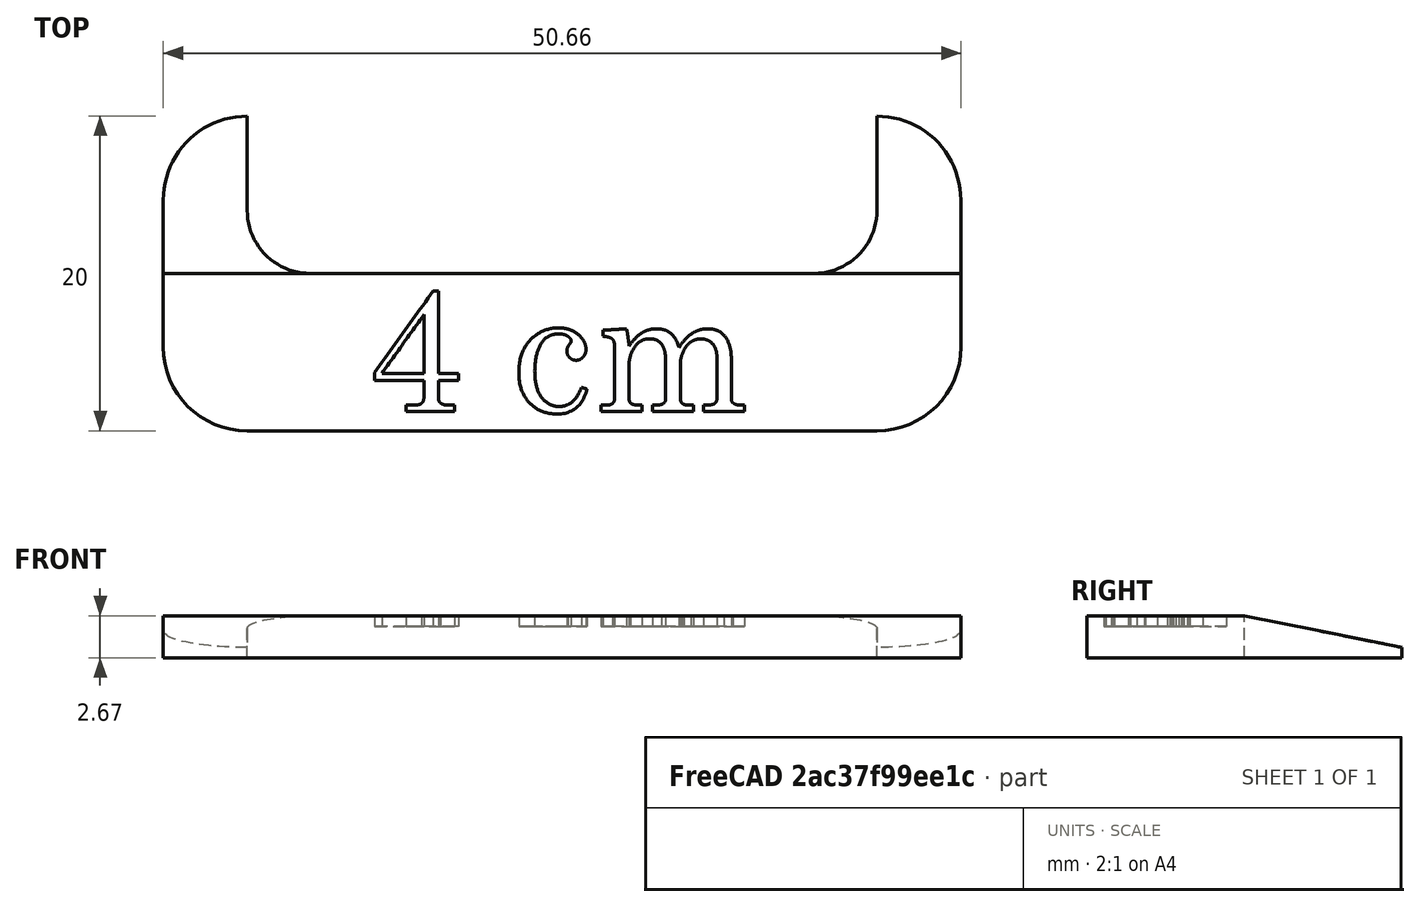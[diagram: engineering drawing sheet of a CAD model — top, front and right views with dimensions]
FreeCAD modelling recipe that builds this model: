
FCSTD DOCUMENT  (FreeCAD 0.20R29603 (Git))
Label: reference-metric-flat
License: All rights reserved
LicenseURL: http://en.wikipedia.org/wiki/All_rights_reserved
objects: Part::Feature×8, PartDesign::Plane×3, Sketcher::SketchObject×3, PartDesign::Pocket×2, App::DocumentObjectGroup×2, App::TextDocument×1, Spreadsheet::Sheet×1, PartDesign::Pad×1, PartDesign::Body×1, Mesh::Feature×1
note: 21 computed .brp shape members not serialized (recipe doc carries the construction recipe); baked Part::Feature solids carry a one-line shape summary decoded from their .brp

FEATURE [App::TextDocument] Text_document  label="Text document"
  Text = 6cm is 40pt Century\n4cm is 32pt Century
FEATURE [Spreadsheet::Sheet] Spreadsheet
  cells = A2=Gap length; B2=gap_l; C2(dim_gap_l)==4 cm; A3=Gap midlength; B3=gap_ml; C3(dim_gap_ml)==dim_gap_l / 2; A4=Measure length; B4=m_l; C4(dim_m_l)==dim_m_ml * 2; A5=Measure midlength; B5=m_ml; C5(dim_m_ml)==dim_gap_ml + dim_fillet_or; A6=Measure width; B6=m_w; C6(dim_m_w)==dim_gap_l / 2; A7=Measure midwidth; B7=m_mw; C7(dim_m_mw)==dim_m_w / 2; A8=Measure height; B8=m_h; C8(dim_m_h)==2 * dim_gap_l / 30; A9=Inner fillet radius; B9=fillet_ir; C9(dim_fillet_ir)==dim_gap_l / 10; A10=Outer fillet radius; B10=fillet_or; C10(dim_fillet_or)==4 * dim_gap_l / 30; A11=Edge height; B11=edge_h; C11(dim_edge_h)==dim_gap_l / 60; A12=Measure X offset; B12=m_x; C12(dim_m_x)==dim_m_w - dim_fillet_ir; A13=Text X offset; B13=text_6cm_x; C13(dim_text_6cm_x)==-15 mm; A14=Text Y offset; B14=text_6cm_y; C14(dim_text_6cm_y)==-1.5 mm; A15=Engrave depth; B15=engrave_h; C15(dim_engrage_h)==dim_m_h / 4; A16=Text 4cm X offset; B16=text_4cm_x; C16(dim_text_4cm_x)==-12 mm; A17=Text 4cm Y offset; B17=text_4cm_y; C17(dim_text_4cm_y)==-1 mm
FEATURE [PartDesign::Plane] DatumPlane  label="BaseXYDatumPlane"
  Length = 60.7331
  MapMode = 5
  ResizeMode = 0
  Support = -> [XY_Plane]
  Width = 60.0664
FEATURE [PartDesign::Plane] DatumPlane001  label="SurfaceXYDatumPlane"
  AttachmentOffset = pos=(0,0,2.66667) rot=(0,0,1;0rad)
  Length = 60.7331
  MapMode = 5
  Placement = pos=(0,0,2.66667) rot=(0,0,1;0rad)
  ResizeMode = 0
  Support = -> [XY_Plane]
  Width = 60.0664
  expr: .AttachmentOffset.Base.z = Spreadsheet.dim_m_h
FEATURE [Sketcher::SketchObject] Sketch  label="OutlineSketch"
  FullyConstrained = true
  MapMode = 5
  Support = -> [DatumPlane]
  expr: Constraints[100] = Spreadsheet.dim_fillet_or
  expr: Constraints[101] = Spreadsheet.dim_fillet_ir
  expr: Constraints[102] = Spreadsheet.dim_m_mw
  expr: Constraints[103] = Spreadsheet.dim_fillet_ir
  expr: Constraints[105] = Spreadsheet.dim_m_x
  expr: Constraints[97] = Spreadsheet.dim_gap_l
  expr: Constraints[98] = Spreadsheet.dim_m_w
  expr: Constraints[99] = Spreadsheet.dim_fillet_or
  sketch-geometry (40):
    g0: LineSegment StartX=-16 StartY=0 StartZ=0 EndX=-2.14051e-11 EndY=0 EndZ=0
    g1: LineSegment StartX=-2.14051e-11 StartY=0 StartZ=0 EndX=16 EndY=0 EndZ=0
    g2: ArcOfCircle CenterX=-16 CenterY=4 CenterZ=0 NormalX=0 NormalY=0 NormalZ=1 AngleXU=0 Radius=4 StartAngle=3.14159 EndAngle=4.71239
    g3: ArcOfCircle CenterX=16 CenterY=4 CenterZ=0 NormalX=0 NormalY=0 NormalZ=1 AngleXU=0 Radius=4 StartAngle=4.71239 EndAngle=6.28319
    g4: ArcOfCircle CenterX=20 CenterY=4.66667 CenterZ=0 NormalX=0 NormalY=0 NormalZ=1 AngleXU=0 Radius=5.33333 StartAngle=0 EndAngle=1.5708
    g5: ArcOfCircle CenterX=-20 CenterY=4.66667 CenterZ=0 NormalX=0 NormalY=0 NormalZ=1 AngleXU=0 Radius=5.33333 StartAngle=1.5708 EndAngle=3.14159
    g6: LineSegment StartX=-25.3333 StartY=4.66667 StartZ=0 EndX=-25.3333 EndY=-4.66667 EndZ=0
    g7: LineSegment StartX=25.3333 StartY=4.66667 StartZ=0 EndX=25.3333 EndY=-4.66667 EndZ=0
    g8: ArcOfCircle CenterX=-20 CenterY=-4.66667 CenterZ=0 NormalX=0 NormalY=0 NormalZ=1 AngleXU=0 Radius=5.33333 StartAngle=3.14159 EndAngle=4.71239
    g9: ArcOfCircle CenterX=20 CenterY=-4.66667 CenterZ=0 NormalX=0 NormalY=0 NormalZ=1 AngleXU=0 Radius=5.33333 StartAngle=4.71239 EndAngle=6.28319
    g10: LineSegment StartX=-20 StartY=-10 StartZ=0 EndX=-2.14051e-11 EndY=-10 EndZ=0
    g11: LineSegment StartX=-2.14051e-11 StartY=-10 StartZ=0 EndX=20 EndY=-10 EndZ=0
    g12: LineSegment StartX=-20 StartY=4 StartZ=0 EndX=-16 EndY=4 EndZ=0
    g13: LineSegment StartX=-16 StartY=4 StartZ=0 EndX=-16 EndY=0 EndZ=0
    g14: LineSegment StartX=-20 StartY=10 StartZ=0 EndX=-2.14051e-11 EndY=10 EndZ=0
    g15: LineSegment StartX=-2.14051e-11 StartY=10 StartZ=0 EndX=20 EndY=10 EndZ=0
    g16: LineSegment StartX=16 StartY=4 StartZ=0 EndX=20 EndY=4 EndZ=0
    g17: LineSegment StartX=16 StartY=4 StartZ=0 EndX=16 EndY=0 EndZ=0
    g18: LineSegment StartX=25.3333 StartY=-4.66667 StartZ=0 EndX=20 EndY=-4.66667 EndZ=0
    g19: LineSegment StartX=20 StartY=-4.66667 StartZ=0 EndX=20 EndY=-10 EndZ=0
    g20: LineSegment StartX=-20 StartY=-4.66667 StartZ=0 EndX=-20 EndY=-10 EndZ=0
    g21: LineSegment StartX=-25.3333 StartY=-4.66667 StartZ=0 EndX=-20 EndY=-4.66667 EndZ=0
    g22: LineSegment StartX=-25.3333 StartY=4.66667 StartZ=0 EndX=-20 EndY=4.66667 EndZ=0
    g23: LineSegment StartX=20 StartY=4.66667 StartZ=0 EndX=25.3333 EndY=4.66667 EndZ=0
    g24: LineSegment StartX=-20 StartY=4 StartZ=0 EndX=-20 EndY=4.66667 EndZ=0
    g25: LineSegment StartX=-20 StartY=4.66667 StartZ=0 EndX=-20 EndY=10 EndZ=0
    g26: LineSegment StartX=20 StartY=4 StartZ=0 EndX=20 EndY=4.66667 EndZ=0
    g27: LineSegment StartX=20 StartY=4.66667 StartZ=0 EndX=20 EndY=10 EndZ=0
    g28: LineSegment StartX=-2.14051e-11 StartY=10 StartZ=0 EndX=-2.14051e-11 EndY=4 EndZ=0
    g29: LineSegment StartX=-2.14051e-11 StartY=4 StartZ=0 EndX=-2.14051e-11 EndY=0 EndZ=0
    g30: LineSegment StartX=-16 StartY=4 StartZ=0 EndX=-2.14051e-11 EndY=4 EndZ=0
    g31: LineSegment StartX=-2.14051e-11 StartY=4 StartZ=0 EndX=16 EndY=4 EndZ=0
    g32: LineSegment StartX=-20 StartY=-4.66667 StartZ=0 EndX=-2.14051e-11 EndY=-4.66667 EndZ=0
    g33: LineSegment StartX=-2.14051e-11 StartY=-4.66667 StartZ=0 EndX=20 EndY=-4.66667 EndZ=0
    g34: LineSegment StartX=-2.14051e-11 StartY=-4.66667 StartZ=0 EndX=-2.14051e-11 EndY=-10 EndZ=0
    g35: LineSegment StartX=-2.14051e-11 StartY=-4.66667 StartZ=0 EndX=-2.14051e-11 EndY=0 EndZ=0
    g36: LineSegment StartX=20 StartY=10 StartZ=0 EndX=25.3333 EndY=10 EndZ=0
    g37: LineSegment StartX=25.3333 StartY=4.66667 StartZ=0 EndX=25.3333 EndY=10 EndZ=0
    g38: LineSegment StartX=20 StartY=-10 StartZ=0 EndX=25.3333 EndY=-10 EndZ=0
    g39: LineSegment StartX=25.3333 StartY=-4.66667 StartZ=0 EndX=25.3333 EndY=-10 EndZ=0
  constraints (107):
    c: Horizontal(g0)
    c: Coincident(g1,g0)
    c: Horizontal(g1)
    c: Coincident(g2,g0)
    c: Coincident(g3,g1)
    c: Coincident(g24,g2)
    c: Coincident(g26,g3)
    c: Coincident(g4,g27)
    c: Coincident(g5,g25)
    c: Coincident(g6,g5)
    c: Vertical(g6)
    c: Coincident(g7,g4)
    c: Vertical(g7)
    c: Coincident(g8,g6)
    c: Coincident(g9,g7)
    c: Coincident(g10,g8)
    c: Horizontal(g10)
    c: Coincident(g11,g10)
    c: Coincident(g11,g9)
    c: Horizontal(g11)
    c: Coincident(g12,g2)
    c: Coincident(g12,g2)
    c: Horizontal(g12)
    c: Coincident(g13,g2)
    c: Coincident(g13,g0)
    c: Vertical(g13)
    c: Coincident(g14,g25)
    c: Horizontal(g14)
    c: Coincident(g28,g14)
    c: Coincident(g29,g0)
    c: Coincident(g15,g14)
    c: Coincident(g15,g27)
    c: Coincident(g16,g3)
    c: Coincident(g16,g3)
    c: Horizontal(g16)
    c: Coincident(g17,g3)
    c: Coincident(g17,g1)
    c: Coincident(g18,g7)
    c: Coincident(g18,g9)
    c: Coincident(g19,g9)
    c: Coincident(g19,g9)
    c: Coincident(g20,g8)
    c: Coincident(g20,g8)
    c: Vertical(g20)
    c: Coincident(g21,g6)
    c: Coincident(g21,g8)
    c: Horizontal(g21)
    c: Coincident(g22,g5)
    c: Coincident(g22,g5)
    c: Horizontal(g22)
    c: Coincident(g23,g4)
    c: Coincident(g23,g4)
    c: Coincident(g24,g25)
    c: Vertical(g24)
    c: Vertical(g25)
    c: Coincident(g26,g27)
    c: Vertical(g26)
    c: Vertical(g27)
    c: Vertical(g19)
    c: Horizontal(g18)
    c: Horizontal(g23)
    c: Vertical(g17)
    c: Coincident(g28,g29)
    c: Vertical(g28)
    c: Vertical(g29)
    c: Coincident(g30,g2)
    c: Coincident(g30,g28)
    c: Horizontal(g30)
    c: Coincident(g31,g28)
    c: Coincident(g31,g3)
    c: Horizontal(g31)
    c: Horizontal(g15)
    c: Coincident(g32,g8)
    c: Horizontal(g32)
    c: Coincident(g33,g32)
    c: Coincident(g33,g9)
    c: Horizontal(g33)
    c: Coincident(g34,g32)
    c: Coincident(g34,g10)
    c: Coincident(g35,g32)
    c: Coincident(g35,g0)
    c: Vertical(g35)
    c: Vertical(g34)
    c: Coincident(g24,g5)
    c: Coincident(g26,g4)
    c: Equal(g14,g15)
    c: Equal(g25,g27)
    c: Coincident(g36,g4)
    c: Horizontal(g36)
    c: Coincident(g37,g4)
    c: Coincident(g37,g36)
    c: Vertical(g37)
    c: Coincident(g38,g9)
    c: Horizontal(g38)
    c: Coincident(g39,g7)
    c: Coincident(g39,g38)
    c: Vertical(g39)
    c: DistanceX(g5,g4) = 40
    c: DistanceY(g38,g36) = 20
    c: DistanceX(g38,g38) = 5.33333
    c: DistanceX(g36,g36) = 5.33333
    c: DistanceY(g13,g13) = 4
    c: DistanceY(g10,g0) = 10
    c: DistanceY(g-1,g28) = 4
    c: DistanceX(g0,g0) = 16
    c: DistanceX(g-1,g1) = 16
    c: DistanceX(g14,g36) = 25.3333
FEATURE [PartDesign::Pad] Pad  label="OutlinePad"
  Direction = (0,0,1)
  Length = 2.66667
  Length2 = 10
  Profile = -> Sketch
  ReferenceAxis = -> Sketch [N_Axis]
  Type = 0
  expr: Length = Spreadsheet.dim_m_h
FEATURE [PartDesign::Plane] DatumPlane002  label="SlopeProfileYZDatumPlane"
  Length = 60
  MapMode = 5
  Placement = pos=(0,0,0) rot=(0.57735,0.57735,0.57735;2.0944rad)
  ResizeMode = 0
  Support = -> [YZ_Plane]
  Width = 60
FEATURE [Sketcher::SketchObject] Sketch001  label="SlopeProfileSketch"
  FullyConstrained = true
  MapMode = 5
  Placement = pos=(0,0,0) rot=(0.57735,0.57735,0.57735;2.0944rad)
  Support = -> [DatumPlane002]
  expr: Constraints[14] = Spreadsheet.dim_m_mw
  expr: Constraints[15] = Spreadsheet.dim_m_h
  expr: Constraints[19] = Spreadsheet.dim_edge_h
  expr: Constraints[2] = Spreadsheet.dim_m_mw
  expr: Constraints[3] = Spreadsheet.dim_edge_h
  sketch-geometry (7):
    g0: LineSegment StartX=10 StartY=0 StartZ=0 EndX=10 EndY=0.666667 EndZ=0
    g1: LineSegment StartX=10 StartY=0.666667 StartZ=0 EndX=0 EndY=2.66667 EndZ=0
    g2: LineSegment StartX=-7e-16 StartY=2.66667 StartZ=0 EndX=-7e-16 EndY=3.33333 EndZ=0
    g3: LineSegment StartX=-7e-16 StartY=3.33333 StartZ=0 EndX=10 EndY=3.33333 EndZ=0
    g4: LineSegment StartX=10 StartY=3.33333 StartZ=0 EndX=10 EndY=2.66667 EndZ=0
    g5: LineSegment StartX=10 StartY=2.66667 StartZ=0 EndX=10 EndY=0.666667 EndZ=0
    g6: LineSegment StartX=-7e-16 StartY=2.66667 StartZ=0 EndX=10 EndY=2.66667 EndZ=0
  constraints (20):
    c: PointOnObject(g0,g-1)
    c: Vertical(g0)
    c: DistanceX(g-1,g0) = 10
    c: DistanceY(g0,g0) = 0.666667
    c: Coincident(g1,g0)
    c: Coincident(g2,g1)
    c: Vertical(g2)
    c: Coincident(g3,g2)
    c: Horizontal(g3)
    c: Coincident(g4,g3)
    c: Coincident(g5,g4)
    c: Coincident(g5,g1)
    c: Vertical(g4)
    c: Vertical(g5)
    c: DistanceX(g3,g3) = 10
    c: DistanceY(g-1,g1) = 2.66667
    c: Coincident(g6,g1)
    c: Coincident(g6,g4)
    c: Horizontal(g6)
    c: DistanceY(g4,g4) = 0.666667
FEATURE [PartDesign::Pocket] Pocket  label="SlopePocket"
  BaseFeature = -> Pad
  Direction = (-1,1e-16,-1e-16)
  Length = 50.6667
  Length2 = 5
  Midplane = true
  Profile = -> Sketch001
  ReferenceAxis = -> Sketch001 [N_Axis]
  Type = 0
  expr: Length = Spreadsheet.dim_m_l
FEATURE [Part::Feature] path22924
  shape: bbox 6.566 x 9.929 x 2e-07 mm, 0 faces, 0 solids (baked)
FEATURE [Part::Feature] path22924001
  shape: bbox 3.686 x 4.899 x 2e-07 mm, 0 faces, 0 solids (baked)
FEATURE [Part::Feature] path22926
  shape: bbox 5.423 x 6.842 x 2e-07 mm, 0 faces, 0 solids (baked)
FEATURE [Part::Feature] path22928
  shape: bbox 11.37 x 6.573 x 2e-07 mm, 0 faces, 0 solids (baked)
FEATURE [App::DocumentObjectGroup] Group  label="6cmVectorGroup"
  Group = -> [path22924,path22924001,path22926,path22928]
FEATURE [Part::Feature] path29369
  shape: bbox 5.325 x 7.645 x 2e-07 mm, 0 faces, 0 solids (baked)
FEATURE [Part::Feature] path29369001
  shape: bbox 2.662 x 3.721 x 2e-07 mm, 0 faces, 0 solids (baked)
FEATURE [Part::Feature] path29371
  shape: bbox 4.338 x 5.474 x 2e-07 mm, 0 faces, 0 solids (baked)
FEATURE [Part::Feature] path29373
  shape: bbox 9.095 x 5.259 x 2e-07 mm, 0 faces, 0 solids (baked)
FEATURE [App::DocumentObjectGroup] Group001  label="4cmVectorGroup"
  Group = -> [path29369,path29369001,path29371,path29373]
FEATURE [Sketcher::SketchObject] Sketch002  label="4cmSketch"
  AttachmentOffset = pos=(-12,-1,0) rot=(0,0,1;0rad)
  FullyConstrained = false
  MapMode = 5
  Placement = pos=(-12,-1,2.66667) rot=(0,0,1;0rad)
  Support = -> [DatumPlane001]
  sketch-geometry (99):
    g0: BSplineCurve PolesCount=2 KnotsCount=2 Degree=1 IsPeriodic=0
    g1: BSplineCurve PolesCount=2 KnotsCount=2 Degree=1 IsPeriodic=0
    g2: BSplineCurve PolesCount=2 KnotsCount=2 Degree=1 IsPeriodic=0
    g3: BSplineCurve PolesCount=2 KnotsCount=2 Degree=1 IsPeriodic=0
    g4: BSplineCurve PolesCount=2 KnotsCount=2 Degree=1 IsPeriodic=0
    g5: BSplineCurve PolesCount=2 KnotsCount=2 Degree=1 IsPeriodic=0
    g6: BSplineCurve PolesCount=3 KnotsCount=2 Degree=2 IsPeriodic=0
    g7: BSplineCurve PolesCount=3 KnotsCount=2 Degree=2 IsPeriodic=0
    g8: BSplineCurve PolesCount=2 KnotsCount=2 Degree=1 IsPeriodic=0
    g9: BSplineCurve PolesCount=2 KnotsCount=2 Degree=1 IsPeriodic=0
    g10: BSplineCurve PolesCount=2 KnotsCount=2 Degree=1 IsPeriodic=0
    g11: BSplineCurve PolesCount=2 KnotsCount=2 Degree=1 IsPeriodic=0
    g12: BSplineCurve PolesCount=2 KnotsCount=2 Degree=1 IsPeriodic=0
    g13: BSplineCurve PolesCount=3 KnotsCount=2 Degree=2 IsPeriodic=0
    g14: BSplineCurve PolesCount=3 KnotsCount=2 Degree=2 IsPeriodic=0
    g15: BSplineCurve PolesCount=2 KnotsCount=2 Degree=1 IsPeriodic=0
    g16: BSplineCurve PolesCount=2 KnotsCount=2 Degree=1 IsPeriodic=0
    g17: BSplineCurve PolesCount=2 KnotsCount=2 Degree=1 IsPeriodic=0
    g18: BSplineCurve PolesCount=2 KnotsCount=2 Degree=1 IsPeriodic=0
    g19: BSplineCurve PolesCount=2 KnotsCount=2 Degree=1 IsPeriodic=0
    g20: BSplineCurve PolesCount=2 KnotsCount=2 Degree=1 IsPeriodic=0
    g21: BSplineCurve PolesCount=2 KnotsCount=2 Degree=1 IsPeriodic=0
    g22: BSplineCurve PolesCount=2 KnotsCount=2 Degree=1 IsPeriodic=0
    g23: BSplineCurve PolesCount=3 KnotsCount=2 Degree=2 IsPeriodic=0
    g24: BSplineCurve PolesCount=3 KnotsCount=2 Degree=2 IsPeriodic=0
    g25: BSplineCurve PolesCount=3 KnotsCount=2 Degree=2 IsPeriodic=0
    g26: BSplineCurve PolesCount=3 KnotsCount=2 Degree=2 IsPeriodic=0
    g27: BSplineCurve PolesCount=3 KnotsCount=2 Degree=2 IsPeriodic=0
    g28: BSplineCurve PolesCount=3 KnotsCount=2 Degree=2 IsPeriodic=0
    g29: BSplineCurve PolesCount=3 KnotsCount=2 Degree=2 IsPeriodic=0
    g30: BSplineCurve PolesCount=3 KnotsCount=2 Degree=2 IsPeriodic=0
    g31: BSplineCurve PolesCount=3 KnotsCount=2 Degree=2 IsPeriodic=0
    g32: BSplineCurve PolesCount=3 KnotsCount=2 Degree=2 IsPeriodic=0
    g33: BSplineCurve PolesCount=3 KnotsCount=2 Degree=2 IsPeriodic=0
    g34: BSplineCurve PolesCount=3 KnotsCount=2 Degree=2 IsPeriodic=0
    g35: BSplineCurve PolesCount=3 KnotsCount=2 Degree=2 IsPeriodic=0
    g36: BSplineCurve PolesCount=3 KnotsCount=2 Degree=2 IsPeriodic=0
    g37: BSplineCurve PolesCount=3 KnotsCount=2 Degree=2 IsPeriodic=0
    g38: BSplineCurve PolesCount=3 KnotsCount=2 Degree=2 IsPeriodic=0
    g39: BSplineCurve PolesCount=3 KnotsCount=2 Degree=2 IsPeriodic=0
    g40: BSplineCurve PolesCount=3 KnotsCount=2 Degree=2 IsPeriodic=0
    g41: BSplineCurve PolesCount=3 KnotsCount=2 Degree=2 IsPeriodic=0
    g42: BSplineCurve PolesCount=3 KnotsCount=2 Degree=2 IsPeriodic=0
    g43: BSplineCurve PolesCount=2 KnotsCount=2 Degree=1 IsPeriodic=0
    g44: BSplineCurve PolesCount=2 KnotsCount=2 Degree=1 IsPeriodic=0
    g45: BSplineCurve PolesCount=3 KnotsCount=2 Degree=2 IsPeriodic=0
    g46: BSplineCurve PolesCount=3 KnotsCount=2 Degree=2 IsPeriodic=0
    g47: BSplineCurve PolesCount=3 KnotsCount=2 Degree=2 IsPeriodic=0
    g48: BSplineCurve PolesCount=3 KnotsCount=2 Degree=2 IsPeriodic=0
    g49: BSplineCurve PolesCount=3 KnotsCount=2 Degree=2 IsPeriodic=0
    g50: BSplineCurve PolesCount=3 KnotsCount=2 Degree=2 IsPeriodic=0
    g51: BSplineCurve PolesCount=3 KnotsCount=2 Degree=2 IsPeriodic=0
    g52: BSplineCurve PolesCount=3 KnotsCount=2 Degree=2 IsPeriodic=0
    g53: BSplineCurve PolesCount=3 KnotsCount=2 Degree=2 IsPeriodic=0
    g54: BSplineCurve PolesCount=2 KnotsCount=2 Degree=1 IsPeriodic=0
    g55: BSplineCurve PolesCount=3 KnotsCount=2 Degree=2 IsPeriodic=0
    g56: BSplineCurve PolesCount=3 KnotsCount=2 Degree=2 IsPeriodic=0
    g57: BSplineCurve PolesCount=2 KnotsCount=2 Degree=1 IsPeriodic=0
    g58: BSplineCurve PolesCount=2 KnotsCount=2 Degree=1 IsPeriodic=0
    g59: BSplineCurve PolesCount=2 KnotsCount=2 Degree=1 IsPeriodic=0
    g60: BSplineCurve PolesCount=2 KnotsCount=2 Degree=1 IsPeriodic=0
    g61: BSplineCurve PolesCount=2 KnotsCount=2 Degree=1 IsPeriodic=0
    g62: BSplineCurve PolesCount=3 KnotsCount=2 Degree=2 IsPeriodic=0
    g63: BSplineCurve PolesCount=3 KnotsCount=2 Degree=2 IsPeriodic=0
    g64: BSplineCurve PolesCount=2 KnotsCount=2 Degree=1 IsPeriodic=0
    g65: BSplineCurve PolesCount=3 KnotsCount=2 Degree=2 IsPeriodic=0
    g66: BSplineCurve PolesCount=3 KnotsCount=2 Degree=2 IsPeriodic=0
    g67: BSplineCurve PolesCount=3 KnotsCount=2 Degree=2 IsPeriodic=0
    g68: BSplineCurve PolesCount=3 KnotsCount=2 Degree=2 IsPeriodic=0
    g69: BSplineCurve PolesCount=3 KnotsCount=2 Degree=2 IsPeriodic=0
    g70: BSplineCurve PolesCount=2 KnotsCount=2 Degree=1 IsPeriodic=0
    g71: BSplineCurve PolesCount=3 KnotsCount=2 Degree=2 IsPeriodic=0
    g72: BSplineCurve PolesCount=3 KnotsCount=2 Degree=2 IsPeriodic=0
    g73: BSplineCurve PolesCount=2 KnotsCount=2 Degree=1 IsPeriodic=0
    g74: BSplineCurve PolesCount=2 KnotsCount=2 Degree=1 IsPeriodic=0
    g75: BSplineCurve PolesCount=2 KnotsCount=2 Degree=1 IsPeriodic=0
    g76: BSplineCurve PolesCount=2 KnotsCount=2 Degree=1 IsPeriodic=0
    g77: BSplineCurve PolesCount=2 KnotsCount=2 Degree=1 IsPeriodic=0
    g78: BSplineCurve PolesCount=3 KnotsCount=2 Degree=2 IsPeriodic=0
    g79: BSplineCurve PolesCount=3 KnotsCount=2 Degree=2 IsPeriodic=0
    g80: BSplineCurve PolesCount=2 KnotsCount=2 Degree=1 IsPeriodic=0
    g81: BSplineCurve PolesCount=3 KnotsCount=2 Degree=2 IsPeriodic=0
    g82: BSplineCurve PolesCount=3 KnotsCount=2 Degree=2 IsPeriodic=0
    g83: BSplineCurve PolesCount=3 KnotsCount=2 Degree=2 IsPeriodic=0
    g84: BSplineCurve PolesCount=3 KnotsCount=2 Degree=2 IsPeriodic=0
    g85: BSplineCurve PolesCount=2 KnotsCount=2 Degree=1 IsPeriodic=0
    g86: BSplineCurve PolesCount=3 KnotsCount=2 Degree=2 IsPeriodic=0
    g87: BSplineCurve PolesCount=3 KnotsCount=2 Degree=2 IsPeriodic=0
    g88: BSplineCurve PolesCount=2 KnotsCount=2 Degree=1 IsPeriodic=0
    g89: BSplineCurve PolesCount=2 KnotsCount=2 Degree=1 IsPeriodic=0
    g90: BSplineCurve PolesCount=2 KnotsCount=2 Degree=1 IsPeriodic=0
    g91: BSplineCurve PolesCount=2 KnotsCount=2 Degree=1 IsPeriodic=0
    g92: BSplineCurve PolesCount=2 KnotsCount=2 Degree=1 IsPeriodic=0
    g93: BSplineCurve PolesCount=3 KnotsCount=2 Degree=2 IsPeriodic=0
    g94: BSplineCurve PolesCount=3 KnotsCount=2 Degree=2 IsPeriodic=0
    g95: BSplineCurve PolesCount=2 KnotsCount=2 Degree=1 IsPeriodic=0
    g96: BSplineCurve PolesCount=3 KnotsCount=2 Degree=2 IsPeriodic=0
    g97: BSplineCurve PolesCount=3 KnotsCount=2 Degree=2 IsPeriodic=0
    g98: BSplineCurve PolesCount=2 KnotsCount=2 Degree=1 IsPeriodic=0
  constraints (99):
    c: Coincident(g0,g1)
    c: Coincident(g1,g2)
    c: Coincident(g2,g3)
    c: Coincident(g3,g4)
    c: Coincident(g4,g5)
    c: Coincident(g5,g6)
    c: Coincident(g6,g7)
    c: Coincident(g7,g8)
    c: Coincident(g8,g9)
    c: Coincident(g9,g10)
    c: Coincident(g10,g11)
    c: Coincident(g11,g12)
    c: Coincident(g12,g13)
    c: Coincident(g13,g14)
    c: Coincident(g14,g15)
    c: Coincident(g15,g16)
    c: Coincident(g16,g17)
    c: Coincident(g17,g18)
    c: Coincident(g18,g0)
    c: Coincident(g19,g20)
    c: Coincident(g20,g21)
    c: Coincident(g21,g19)
    c: Coincident(g22,g23)
    c: Coincident(g23,g24)
    c: Coincident(g24,g25)
    c: Coincident(g25,g26)
    c: Coincident(g26,g27)
    c: Coincident(g27,g28)
    c: Coincident(g28,g29)
    c: Coincident(g29,g30)
    c: Coincident(g30,g31)
    c: Coincident(g31,g32)
    c: Coincident(g32,g33)
    c: Coincident(g33,g34)
    c: Coincident(g34,g35)
    c: Coincident(g35,g36)
    c: Coincident(g36,g37)
    c: Coincident(g37,g38)
    c: Coincident(g38,g39)
    c: Coincident(g39,g40)
    c: Coincident(g40,g41)
    c: Coincident(g41,g42)
    c: Coincident(g42,g43)
    c: Coincident(g43,g22)
    c: Coincident(g44,g45)
    c: Coincident(g45,g46)
    c: Coincident(g46,g47)
    c: Coincident(g47,g48)
    c: Coincident(g48,g49)
    c: Coincident(g49,g50)
    c: Coincident(g50,g51)
    c: Coincident(g51,g52)
    c: Coincident(g52,g53)
    c: Coincident(g53,g54)
    c: Coincident(g54,g55)
    c: Coincident(g55,g56)
    c: Coincident(g56,g57)
    c: Coincident(g57,g58)
    c: Coincident(g58,g59)
    c: Coincident(g59,g60)
    c: Coincident(g60,g61)
    c: Coincident(g61,g62)
    c: Coincident(g62,g63)
    c: Coincident(g63,g64)
    c: Coincident(g64,g65)
    c: Coincident(g65,g66)
    c: Coincident(g66,g67)
    c: Coincident(g67,g68)
    c: Coincident(g68,g69)
    c: Coincident(g69,g70)
    c: Coincident(g70,g71)
    c: Coincident(g71,g72)
    c: Coincident(g72,g73)
    c: Coincident(g73,g74)
    c: Coincident(g74,g75)
    c: Coincident(g75,g76)
    c: Coincident(g76,g77)
    c: Coincident(g77,g78)
    c: Coincident(g78,g79)
    c: Coincident(g79,g80)
    c: Coincident(g80,g81)
    c: Coincident(g81,g82)
    c: Coincident(g82,g83)
    c: Coincident(g83,g84)
    c: Coincident(g84,g85)
    c: Coincident(g85,g86)
    c: Coincident(g86,g87)
    c: Coincident(g87,g88)
    c: Coincident(g88,g89)
    c: Coincident(g89,g90)
    c: Coincident(g90,g91)
    c: Coincident(g91,g92)
    c: Coincident(g92,g93)
    c: Coincident(g93,g94)
    c: Coincident(g94,g95)
    c: Coincident(g95,g96)
    c: Coincident(g96,g97)
    c: Coincident(g97,g98)
    c: Coincident(g98,g44)
FEATURE [PartDesign::Pocket] Pocket001  label="4cmPocket"
  BaseFeature = -> Pocket
  Direction = (0,0,-1)
  Length = 0.666667
  Length2 = 5
  Profile = -> Sketch002
  ReferenceAxis = -> Sketch002 [N_Axis]
  Type = 0
  expr: Length = Spreadsheet.dim_engrage_h
FEATURE [PartDesign::Body] Body
  Group = -> [DatumPlane,DatumPlane001,Sketch,Pad,DatumPlane002,Sketch001,Pocket,Sketch002,Pocket001]
  Origin = -> Origin
  Tip = -> Pocket001
FEATURE [Mesh::Feature] Mesh  label="Body (Meshed)"
